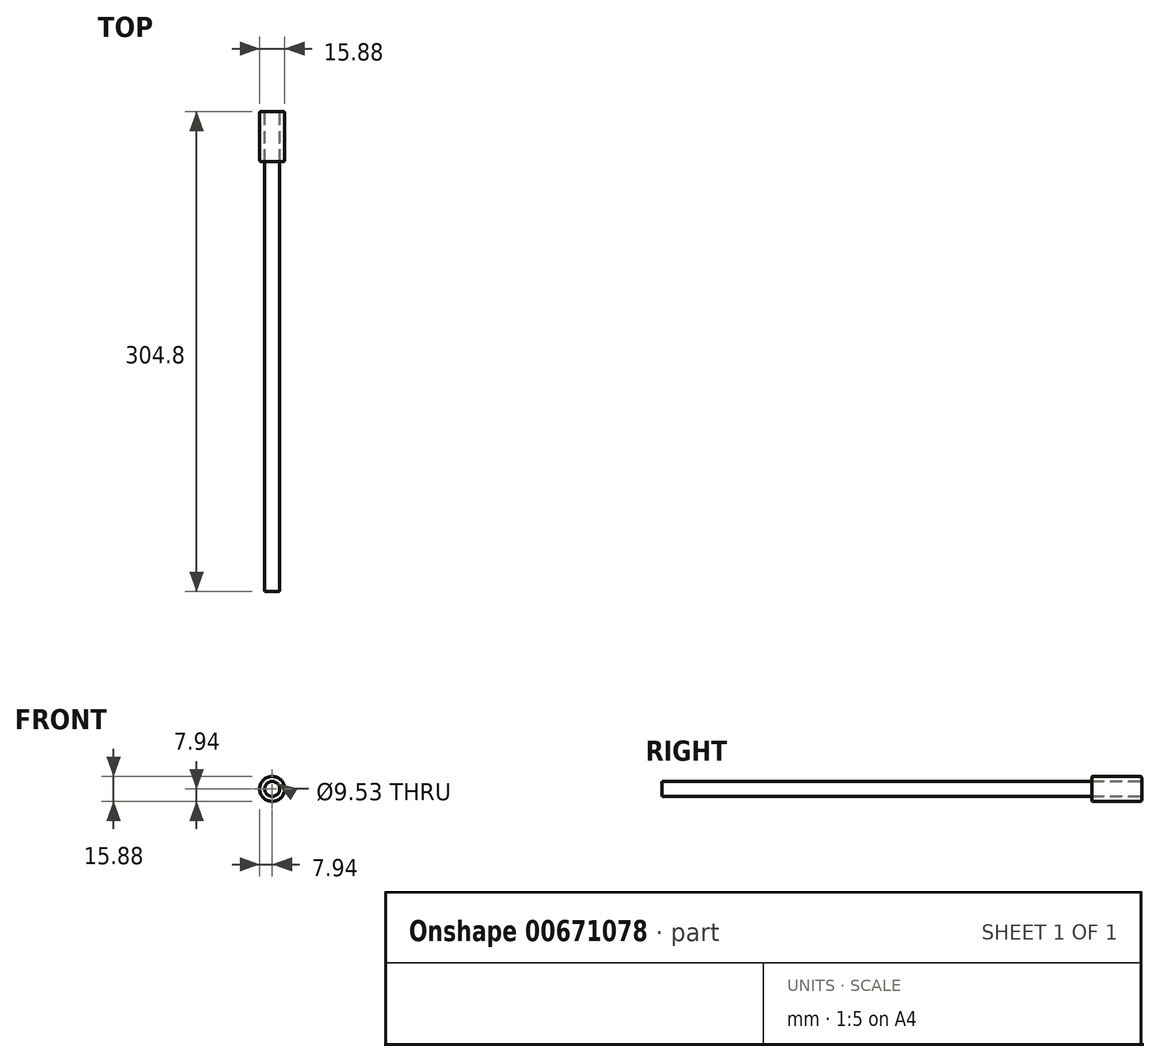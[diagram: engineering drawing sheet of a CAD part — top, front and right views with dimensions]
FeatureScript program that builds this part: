
annotation { "Feature Type Name" : "Feature", "Feature Type Description" : "" }
export const myFeature = defineFeature(function(context is Context, id is Id, definition is map)
    precondition{}
    {
        {
            var Q0;
            Q0=qCreatedBy(makeId("Front.planeOp"),FACE);
            var sketch = newSketch(context, id + "F0", { "sketchPlane" : qUnion([Q0])});
            skCircle(sketch, "E0", {"center": v(0, 0) * mm, "radius": 7.94 * mm});
            skSolve(sketch);
        }
        {
            var Q0;
            Q0 = qSketchRegion(id + "F0", true);
            extrude(context, id + "F1", {"entities" : qUnion([Q0]), "depth" : 31.75 * mm, "offsetDistance" : 25.4 * mm});
        }
        {
            var Q0;
            Q0=makeQuery(id+"F1.opExtrude","CAP_FACE",FACE,{"disambiguationData":[OSD([sQuery(id+"F0.wireOp",EDGE,"E0")])],"isStart":false});
            var sketch = newSketch(context, id + "F2", { "sketchPlane" : qUnion([Q0])});
            skCircle(sketch, "E1", {"center": v(0, 0) * mm, "radius": 4.76 * mm});
            skSolve(sketch);
        }
        {
            var Q0;
            Q0 = qSketchRegion(id + "F2", true);
            extrude(context, id + "F3", {"entities" : qUnion([Q0]), "operationType" : NewBodyOperationType.REMOVE, "endBound" : BoundingType.THROUGH_ALL, "oppositeDirection" : true, "depth" : 25.4 * mm, "offsetDistance" : 25.4 * mm});
        }
        {
            var Q0;
            Q0=makeQuery(id+"F1.opExtrude","CAP_FACE",FACE,{"disambiguationData":[OSD([sQuery(id+"F0.wireOp",EDGE,"E0")])],"isStart":false});
            var Q1;
            Q1=makeQuery(id+"F1.opExtrude","CAP_FACE",FACE,{"disambiguationData":[OSD([sQuery(id+"F0.wireOp",EDGE,"E0")])],"isStart":true});
            fillet(context, id + "F4", {"entities" : qUnion([Q0, Q1]), "radius" : 0.8 * mm, "tangentPropagation" : true, "allowEdgeOverflow" : false});
        }
        {
            var Q0;
            Q0=qCreatedBy(makeId("Front.planeOp"),FACE);
            var sketch = newSketch(context, id + "F5", { "sketchPlane" : qUnion([Q0])});
            skCircle(sketch, "E2.0", {"center": v(0, 0) * mm, "radius": 4.76 * mm});
            skSolve(sketch);
        }
        {
            var Q0;
            Q0 = qSketchRegion(id + "F5", true);
            extrude(context, id + "F6", {"entities" : qUnion([Q0]), "depth" : 304.8 * mm, "offsetDistance" : 25.4 * mm});
        }
    });
